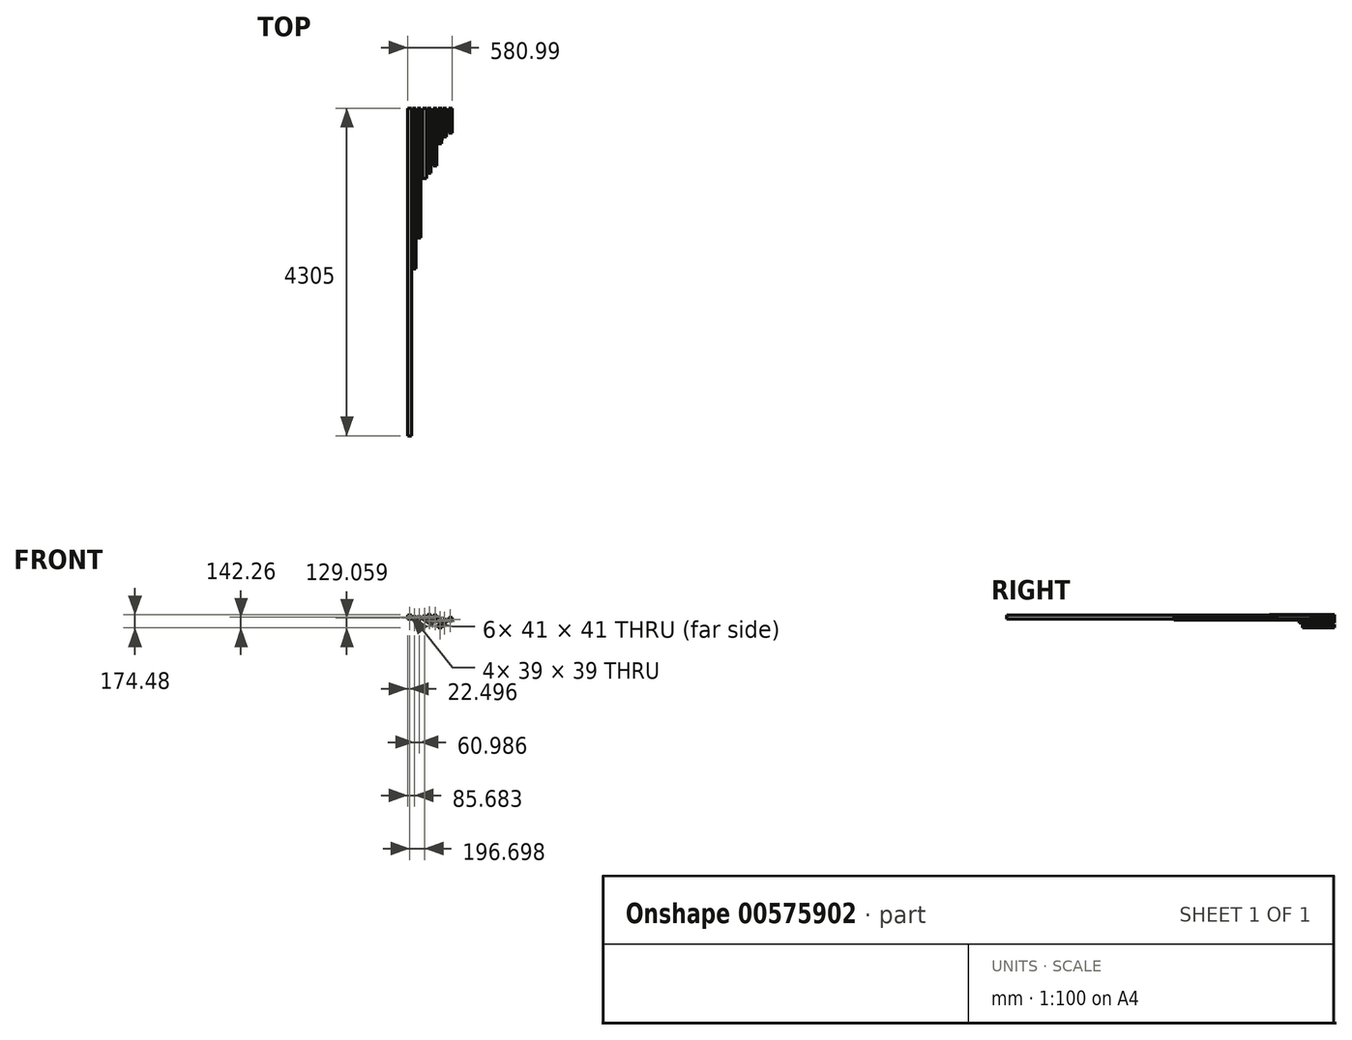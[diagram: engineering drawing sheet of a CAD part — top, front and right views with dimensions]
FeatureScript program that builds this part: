
annotation { "Feature Type Name" : "Feature", "Feature Type Description" : "" }
export const myFeature = defineFeature(function(context is Context, id is Id, definition is map)
    precondition{}
    {
        {
            var Q0;
            Q0=qCreatedBy(makeId("Front.planeOp"),FACE);
            var sketch = newSketch(context, id + "F0", { "sketchPlane" : qUnion([Q0])});
            skLineSegment(sketch, "E0.bottom", {"start": v(0, 45) * mm, "end": v(45, 45) * mm});
            skLineSegment(sketch, "E0.top", {"start": v(0, 0) * mm, "end": v(45, 0) * mm});
            skLineSegment(sketch, "E0.left", {"start": v(0, 45) * mm, "end": v(0, 0) * mm});
            skLineSegment(sketch, "E0.right", {"start": v(45, 45) * mm, "end": v(45, 0) * mm});
            skLineSegment(sketch, "E1.0", {"start": v(3, 42) * mm, "end": v(42, 42) * mm});
            skLineSegment(sketch, "E1.1", {"start": v(3, 42) * mm, "end": v(3, 3) * mm});
            skLineSegment(sketch, "E1.2", {"start": v(3, 3) * mm, "end": v(42, 3) * mm});
            skLineSegment(sketch, "E1.3", {"start": v(42, 42) * mm, "end": v(42, 3) * mm});
            skPoint(sketch, "E2.top.start.orphan", {"position": v(-75.29, 9.72) * mm});
            skLineSegment(sketch, "E3.bottom", {"start": v(-75.29, 54.72) * mm, "end": v(-30.29, 54.72) * mm});
            skLineSegment(sketch, "E3.top", {"start": v(-75.29, 9.72) * mm, "end": v(-30.29, 9.72) * mm});
            skLineSegment(sketch, "E3.left", {"start": v(-75.29, 54.72) * mm, "end": v(-75.29, 9.72) * mm});
            skLineSegment(sketch, "E3.right", {"start": v(-30.29, 54.72) * mm, "end": v(-30.29, 9.72) * mm});
            skLineSegment(sketch, "E4.0", {"start": v(-72.29, 51.72) * mm, "end": v(-33.29, 51.72) * mm});
            skLineSegment(sketch, "E4.1", {"start": v(-72.29, 51.72) * mm, "end": v(-72.29, 12.72) * mm});
            skLineSegment(sketch, "E4.2", {"start": v(-72.29, 12.72) * mm, "end": v(-33.29, 12.72) * mm});
            skLineSegment(sketch, "E4.3", {"start": v(-33.29, 51.72) * mm, "end": v(-33.29, 12.72) * mm});
            skLineSegment(sketch, "E5.bottom", {"start": v(-136.6, 35) * mm, "end": v(-91.6, 35) * mm});
            skLineSegment(sketch, "E5.top", {"start": v(-136.6, -10) * mm, "end": v(-91.6, -10) * mm});
            skLineSegment(sketch, "E5.left", {"start": v(-136.6, 35) * mm, "end": v(-136.6, -10) * mm});
            skLineSegment(sketch, "E5.right", {"start": v(-91.6, 35) * mm, "end": v(-91.6, -10) * mm});
            skLineSegment(sketch, "E6.0", {"start": v(-133.6, 32) * mm, "end": v(-94.6, 32) * mm});
            skLineSegment(sketch, "E6.1", {"start": v(-133.6, 32) * mm, "end": v(-133.6, -7) * mm});
            skLineSegment(sketch, "E6.2", {"start": v(-133.6, -7) * mm, "end": v(-94.6, -7) * mm});
            skLineSegment(sketch, "E6.3", {"start": v(-94.6, 32) * mm, "end": v(-94.6, -7) * mm});
            skLineSegment(sketch, "E7.bottom", {"start": v(-209.12, 30.36) * mm, "end": v(-164.12, 30.36) * mm});
            skLineSegment(sketch, "E7.top", {"start": v(-209.12, -14.64) * mm, "end": v(-164.12, -14.64) * mm});
            skLineSegment(sketch, "E7.left", {"start": v(-209.12, 30.36) * mm, "end": v(-209.12, -14.64) * mm});
            skLineSegment(sketch, "E7.right", {"start": v(-164.12, 30.36) * mm, "end": v(-164.12, -14.64) * mm});
            skLineSegment(sketch, "E8.0", {"start": v(-207.12, 28.36) * mm, "end": v(-166.12, 28.36) * mm});
            skLineSegment(sketch, "E8.1", {"start": v(-207.12, 28.36) * mm, "end": v(-207.12, -12.64) * mm});
            skLineSegment(sketch, "E8.2", {"start": v(-207.12, -12.64) * mm, "end": v(-166.12, -12.64) * mm});
            skLineSegment(sketch, "E8.3", {"start": v(-166.12, 28.36) * mm, "end": v(-166.12, -12.64) * mm});
            skLineSegment(sketch, "E9.bottom", {"start": v(-270.1, 31.8) * mm, "end": v(-225.1, 31.8) * mm});
            skLineSegment(sketch, "E9.top", {"start": v(-270.1, -13.2) * mm, "end": v(-225.1, -13.2) * mm});
            skLineSegment(sketch, "E9.left", {"start": v(-270.1, 31.8) * mm, "end": v(-270.1, -13.2) * mm});
            skLineSegment(sketch, "E9.right", {"start": v(-225.1, 31.8) * mm, "end": v(-225.1, -13.2) * mm});
            skLineSegment(sketch, "E10.0", {"start": v(-268.1, 29.8) * mm, "end": v(-227.1, 29.8) * mm});
            skLineSegment(sketch, "E10.1", {"start": v(-268.1, 29.8) * mm, "end": v(-268.1, -11.2) * mm});
            skLineSegment(sketch, "E10.2", {"start": v(-268.1, -11.2) * mm, "end": v(-227.1, -11.2) * mm});
            skLineSegment(sketch, "E10.3", {"start": v(-227.1, 29.8) * mm, "end": v(-227.1, -11.2) * mm});
            skLineSegment(sketch, "E11.bottom", {"start": v(65.16, -8.39) * mm, "end": v(110.16, -8.39) * mm});
            skLineSegment(sketch, "E11.top", {"start": v(65.16, -53.39) * mm, "end": v(110.16, -53.39) * mm});
            skLineSegment(sketch, "E11.left", {"start": v(65.16, -8.39) * mm, "end": v(65.16, -53.39) * mm});
            skLineSegment(sketch, "E11.right", {"start": v(110.16, -8.39) * mm, "end": v(110.16, -53.39) * mm});
            skLineSegment(sketch, "E12.0", {"start": v(67.16, -10.39) * mm, "end": v(108.16, -10.39) * mm});
            skLineSegment(sketch, "E12.1", {"start": v(67.16, -10.39) * mm, "end": v(67.16, -51.39) * mm});
            skLineSegment(sketch, "E12.2", {"start": v(67.16, -51.39) * mm, "end": v(108.16, -51.39) * mm});
            skLineSegment(sketch, "E12.3", {"start": v(108.16, -10.39) * mm, "end": v(108.16, -51.39) * mm});
            skLineSegment(sketch, "E13.bottom", {"start": v(126.48, -11.44) * mm, "end": v(171.48, -11.44) * mm});
            skLineSegment(sketch, "E13.top", {"start": v(126.48, -56.44) * mm, "end": v(171.48, -56.44) * mm});
            skLineSegment(sketch, "E13.left", {"start": v(126.48, -11.44) * mm, "end": v(126.48, -56.44) * mm});
            skLineSegment(sketch, "E13.right", {"start": v(171.48, -11.44) * mm, "end": v(171.48, -56.44) * mm});
            skLineSegment(sketch, "E14.0", {"start": v(128.48, -13.44) * mm, "end": v(169.48, -13.44) * mm});
            skLineSegment(sketch, "E14.1", {"start": v(128.48, -13.44) * mm, "end": v(128.48, -54.44) * mm});
            skLineSegment(sketch, "E14.2", {"start": v(128.48, -54.44) * mm, "end": v(169.48, -54.44) * mm});
            skLineSegment(sketch, "E14.3", {"start": v(169.48, -13.44) * mm, "end": v(169.48, -54.44) * mm});
            skLineSegment(sketch, "E15.bottom", {"start": v(-333.3, 45) * mm, "end": v(-288.3, 45) * mm});
            skLineSegment(sketch, "E15.top", {"start": v(-333.3, 0) * mm, "end": v(-288.3, 0) * mm});
            skLineSegment(sketch, "E15.left", {"start": v(-333.3, 45) * mm, "end": v(-333.3, 0) * mm});
            skLineSegment(sketch, "E15.right", {"start": v(-288.3, 45) * mm, "end": v(-288.3, 0) * mm});
            skLineSegment(sketch, "E16.0", {"start": v(-330.3, 42) * mm, "end": v(-291.3, 42) * mm});
            skLineSegment(sketch, "E16.1", {"start": v(-330.3, 42) * mm, "end": v(-330.3, 3) * mm});
            skLineSegment(sketch, "E16.2", {"start": v(-330.3, 3) * mm, "end": v(-291.3, 3) * mm});
            skLineSegment(sketch, "E16.3", {"start": v(-291.3, 42) * mm, "end": v(-291.3, 3) * mm});
            skLineSegment(sketch, "E17.bottom", {"start": v(-401.14, 59.64) * mm, "end": v(-356.14, 59.64) * mm});
            skLineSegment(sketch, "E17.top", {"start": v(-401.14, 14.64) * mm, "end": v(-356.14, 14.64) * mm});
            skLineSegment(sketch, "E17.left", {"start": v(-401.14, 59.64) * mm, "end": v(-401.14, 14.64) * mm});
            skLineSegment(sketch, "E17.right", {"start": v(-356.14, 59.64) * mm, "end": v(-356.14, 14.64) * mm});
            skLineSegment(sketch, "E18.0", {"start": v(-399.14, 57.64) * mm, "end": v(-358.14, 57.64) * mm});
            skLineSegment(sketch, "E18.1", {"start": v(-399.14, 57.64) * mm, "end": v(-399.14, 16.64) * mm});
            skLineSegment(sketch, "E18.2", {"start": v(-399.14, 16.64) * mm, "end": v(-358.14, 16.64) * mm});
            skLineSegment(sketch, "E18.3", {"start": v(-358.14, 57.64) * mm, "end": v(-358.14, 16.64) * mm});
            skLineSegment(sketch, "E19.bottom", {"start": v(202.7, 15.9) * mm, "end": v(247.7, 15.9) * mm});
            skLineSegment(sketch, "E19.top", {"start": v(202.7, -29.1) * mm, "end": v(247.7, -29.1) * mm});
            skLineSegment(sketch, "E19.left", {"start": v(202.7, 15.9) * mm, "end": v(202.7, -29.1) * mm});
            skLineSegment(sketch, "E19.right", {"start": v(247.7, 15.9) * mm, "end": v(247.7, -29.1) * mm});
            skLineSegment(sketch, "E20.0", {"start": v(204.7, 13.9) * mm, "end": v(245.7, 13.9) * mm});
            skLineSegment(sketch, "E20.1", {"start": v(204.7, 13.9) * mm, "end": v(204.7, -27.1) * mm});
            skLineSegment(sketch, "E20.2", {"start": v(204.7, -27.1) * mm, "end": v(245.7, -27.1) * mm});
            skLineSegment(sketch, "E20.3", {"start": v(245.7, 13.9) * mm, "end": v(245.7, -27.1) * mm});
            skLineSegment(sketch, "E21.bottom", {"start": v(-465.86, 22.61) * mm, "end": v(-420.86, 22.61) * mm});
            skLineSegment(sketch, "E21.top", {"start": v(-465.86, -22.39) * mm, "end": v(-420.86, -22.39) * mm});
            skLineSegment(sketch, "E21.left", {"start": v(-465.86, 22.61) * mm, "end": v(-465.86, -22.39) * mm});
            skLineSegment(sketch, "E21.right", {"start": v(-420.86, 22.61) * mm, "end": v(-420.86, -22.39) * mm});
            skLineSegment(sketch, "E22.0", {"start": v(-463.86, 20.61) * mm, "end": v(-422.86, 20.61) * mm});
            skLineSegment(sketch, "E22.1", {"start": v(-463.86, 20.61) * mm, "end": v(-463.86, -20.39) * mm});
            skLineSegment(sketch, "E22.2", {"start": v(-463.86, -20.39) * mm, "end": v(-422.86, -20.39) * mm});
            skLineSegment(sketch, "E22.3", {"start": v(-422.86, 20.61) * mm, "end": v(-422.86, -20.39) * mm});
            skLineSegment(sketch, "E23.bottom", {"start": v(66.51, -74.76) * mm, "end": v(111.51, -74.76) * mm});
            skLineSegment(sketch, "E23.top", {"start": v(66.51, -119.76) * mm, "end": v(111.51, -119.76) * mm});
            skLineSegment(sketch, "E23.left", {"start": v(66.51, -74.76) * mm, "end": v(66.51, -119.76) * mm});
            skLineSegment(sketch, "E23.right", {"start": v(111.51, -74.76) * mm, "end": v(111.51, -119.76) * mm});
            skLineSegment(sketch, "E24.0", {"start": v(68.51, -76.76) * mm, "end": v(109.51, -76.76) * mm});
            skLineSegment(sketch, "E24.1", {"start": v(68.51, -76.76) * mm, "end": v(68.51, -117.76) * mm});
            skLineSegment(sketch, "E24.2", {"start": v(68.51, -117.76) * mm, "end": v(109.51, -117.76) * mm});
            skLineSegment(sketch, "E24.3", {"start": v(109.51, -76.76) * mm, "end": v(109.51, -117.76) * mm});
            skSolve(sketch);
        }
        {
            var Q0;
            Q0=makeQuery(id+"F0.imprint","IMPRINT",FACE,{"disambiguationData":[TD([[makeQuery(id+"F0.imprint","IMPRINT",EDGE,{"derivedFrom":sQuery(id+"F0.wireOp",EDGE,"E0.bottom")}),-1.0]])]});
            extrude(context, id + "F1", {"entities" : qUnion([Q0]), "depth" : 755 * mm, "offsetDistance" : 25 * mm});
        }
        {
            var Q0;
            Q0=makeQuery(id+"F0.imprint","IMPRINT",FACE,{"disambiguationData":[TD([[makeQuery(id+"F0.imprint","IMPRINT",EDGE,{"derivedFrom":sQuery(id+"F0.wireOp",EDGE,"E3.bottom")}),-1.0]])]});
            extrude(context, id + "F2", {"entities" : qUnion([Q0]), "depth" : 850 * mm, "offsetDistance" : 25 * mm});
        }
        {
            var Q0;
            Q0=makeQuery(id+"F0.imprint","IMPRINT",FACE,{"disambiguationData":[TD([[makeQuery(id+"F0.imprint","IMPRINT",EDGE,{"derivedFrom":sQuery(id+"F0.wireOp",EDGE,"E5.bottom")}),-1.0]])]});
            extrude(context, id + "F3", {"entities" : qUnion([Q0]), "depth" : 920 * mm, "offsetDistance" : 25 * mm});
        }
        {
            var Q0;
            Q0=makeQuery(id+"F0.imprint","IMPRINT",FACE,{"disambiguationData":[TD([[makeQuery(id+"F0.imprint","IMPRINT",EDGE,{"derivedFrom":sQuery(id+"F0.wireOp",EDGE,"E7.bottom")}),-1.0]])]});
            extrude(context, id + "F4", {"entities" : qUnion([Q0]), "depth" : 1700 * mm, "offsetDistance" : 25 * mm});
        }
        {
            var Q0;
            Q0=makeQuery(id+"F0.imprint","IMPRINT",FACE,{"disambiguationData":[TD([[makeQuery(id+"F0.imprint","IMPRINT",EDGE,{"derivedFrom":sQuery(id+"F0.wireOp",EDGE,"E9.bottom")}),-1.0]])]});
            extrude(context, id + "F5", {"entities" : qUnion([Q0]), "depth" : 2110 * mm, "offsetDistance" : 25 * mm});
        }
        {
            var Q0;
            Q0=makeQuery(id+"F0.imprint","IMPRINT",FACE,{"disambiguationData":[TD([[makeQuery(id+"F0.imprint","IMPRINT",EDGE,{"derivedFrom":sQuery(id+"F0.wireOp",EDGE,"E11.bottom")}),-1.0]])]});
            extrude(context, id + "F6", {"entities" : qUnion([Q0]), "depth" : 465 * mm, "offsetDistance" : 25 * mm});
        }
        {
            var Q0;
            Q0=makeQuery(id+"F0.imprint","IMPRINT",FACE,{"disambiguationData":[TD([[makeQuery(id+"F0.imprint","IMPRINT",EDGE,{"derivedFrom":sQuery(id+"F0.wireOp",EDGE,"E13.bottom")}),-1.0]])]});
            extrude(context, id + "F7", {"entities" : qUnion([Q0]), "depth" : 375 * mm, "offsetDistance" : 25 * mm});
        }
        {
            var Q0;
            Q0=makeQuery(id+"F0.imprint","IMPRINT",FACE,{"disambiguationData":[TD([[makeQuery(id+"F0.imprint","IMPRINT",EDGE,{"derivedFrom":sQuery(id+"F0.wireOp",EDGE,"E15.bottom")}),-1.0]])]});
            extrude(context, id + "F8", {"entities" : qUnion([Q0]), "depth" : 4305 * mm, "offsetDistance" : 25 * mm});
        }
        {
            var Q0;
            Q0=makeQuery(id+"F0.imprint","IMPRINT",FACE,{"disambiguationData":[TD([[makeQuery(id+"F0.imprint","IMPRINT",EDGE,{"derivedFrom":sQuery(id+"F0.wireOp",EDGE,"E19.bottom")}),-1.0]])]});
            extrude(context, id + "F9", {"entities" : qUnion([Q0]), "depth" : 325 * mm, "offsetDistance" : 25 * mm});
        }
        {
            var Q0;
            Q0=makeQuery(id+"F0.imprint","IMPRINT",FACE,{"disambiguationData":[TD([[makeQuery(id+"F0.imprint","IMPRINT",EDGE,{"derivedFrom":sQuery(id+"F0.wireOp",EDGE,"E23.bottom")}),-1.0]])]});
            extrude(context, id + "F10", {"entities" : qUnion([Q0]), "depth" : 420 * mm, "offsetDistance" : 25 * mm});
        }
    });
